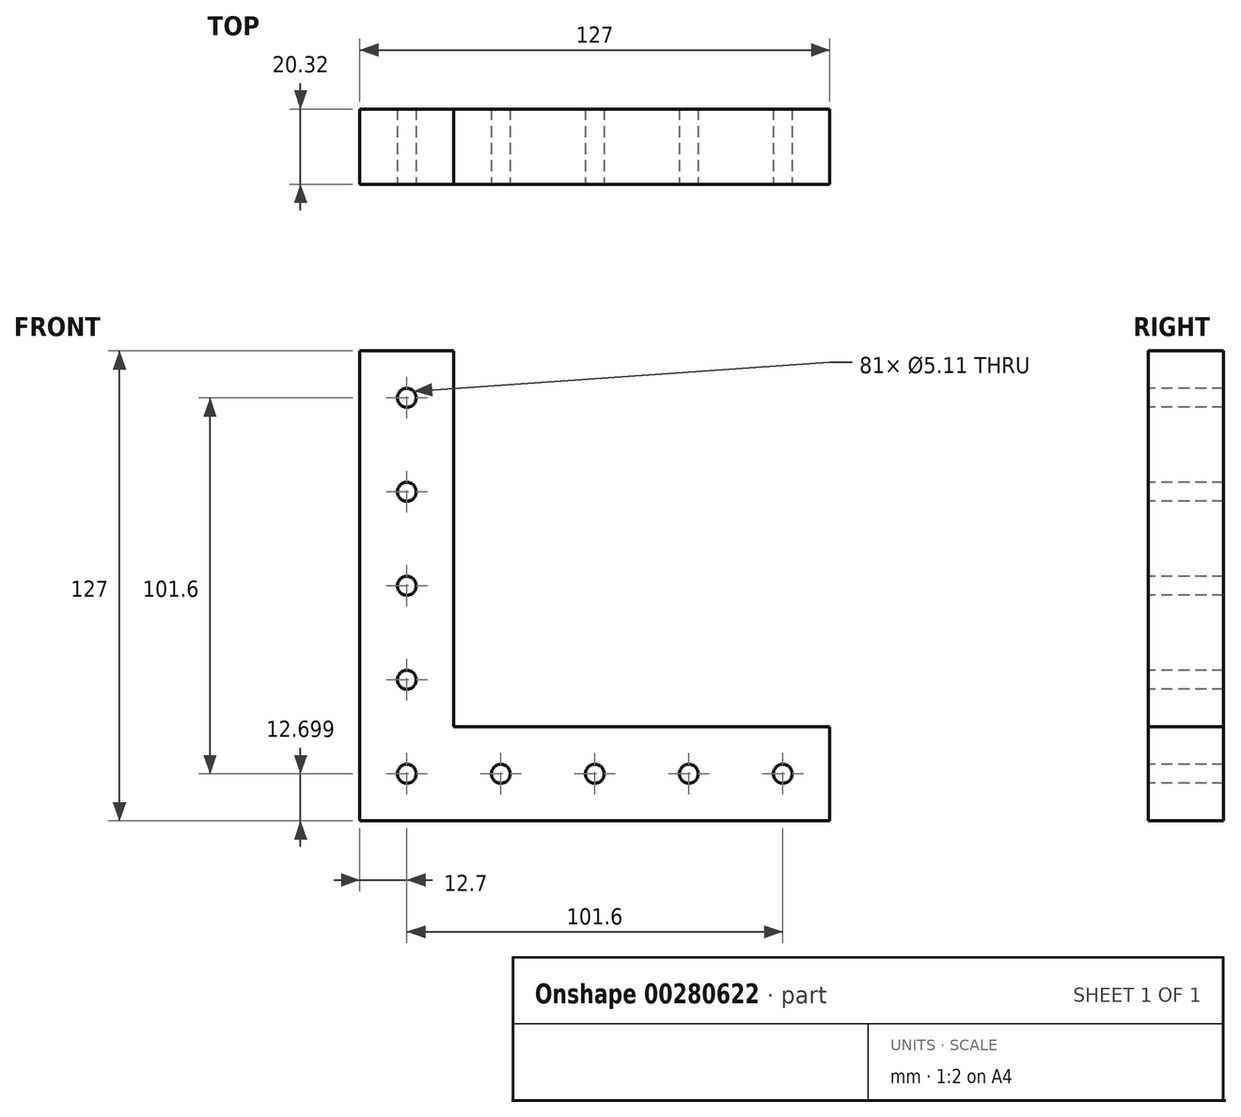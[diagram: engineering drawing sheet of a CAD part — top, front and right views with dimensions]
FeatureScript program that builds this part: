
annotation { "Feature Type Name" : "Feature", "Feature Type Description" : "" }
export const myFeature = defineFeature(function(context is Context, id is Id, definition is map)
    precondition{}
    {
        {
            var Q0;
            Q0=qCreatedBy(makeId("Front.planeOp"),FACE);
            var sketch = newSketch(context, id + "F0", { "sketchPlane" : qUnion([Q0])});
            skLineSegment(sketch, "E0", {"start": v(-127, 49.39) * mm, "end": v(-127, -77.61) * mm});
            skLineSegment(sketch, "E1", {"start": v(-127, -77.61) * mm, "end": v(0, -77.61) * mm});
            skLineSegment(sketch, "E2", {"start": v(0, -77.61) * mm, "end": v(0, -52.21) * mm});
            skLineSegment(sketch, "E3", {"start": v(0, -52.21) * mm, "end": v(-101.6, -52.21) * mm});
            skLineSegment(sketch, "E4", {"start": v(-101.6, -52.21) * mm, "end": v(-101.6, 49.39) * mm});
            skLineSegment(sketch, "E5", {"start": v(-101.6, 49.39) * mm, "end": v(-127, 49.39) * mm});
            skSolve(sketch);
        }
        {
            var Q0;
            Q0=makeQuery(id+"F0.imprint","IMPRINT",FACE,{"disambiguationData":[TD([[makeQuery(id+"F0.imprint","IMPRINT",EDGE,{"derivedFrom":sQuery(id+"F0.wireOp",EDGE,"E0")}),1.0]])]});
            extrude(context, id + "F1", {"entities" : qUnion([Q0]), "depth" : 20.32 * mm});
        }
        {
            var Q0;
            Q0=makeQuery(id+"F1.opExtrude","CAP_FACE",FACE,{"disambiguationData":[OSD([sQuery(id+"F0.wireOp",EDGE,"E0"),sQuery(id+"F0.wireOp",EDGE,"E1"),sQuery(id+"F0.wireOp",EDGE,"E2"),sQuery(id+"F0.wireOp",EDGE,"E3"),sQuery(id+"F0.wireOp",EDGE,"E4"),sQuery(id+"F0.wireOp",EDGE,"E5")])],"isStart":false});
            var sketch = newSketch(context, id + "F2", { "sketchPlane" : qUnion([Q0])});
            skCircle(sketch, "E6", {"center": v(-12.7, -64.91) * mm, "radius": 2.55 * mm});
            skCircle(sketch, "E7.1.0.0", {"center": v(-38.1, -64.91) * mm, "radius": 2.55 * mm});
            skCircle(sketch, "E7.2.0.0", {"center": v(-63.5, -64.91) * mm, "radius": 2.55 * mm});
            skCircle(sketch, "E7.3.0.0", {"center": v(-88.9, -64.91) * mm, "radius": 2.55 * mm});
            skCircle(sketch, "E7.4.0.0", {"center": v(-114.3, -64.91) * mm, "radius": 2.55 * mm});
            skLineSegment(sketch, "E7.direction1", {"start": v(-12.7, -64.91) * mm, "end": v(-38.1, -64.91) * mm, "construction": true});
            skLineSegment(sketch, "E7.direction2", {"start": v(-12.7, -64.91) * mm, "end": v(-12.7, -39.51) * mm, "construction": true});
            skCircle(sketch, "E8.0.1.0", {"center": v(-114.3, -39.51) * mm, "radius": 2.55 * mm});
            skCircle(sketch, "E8.0.2.0", {"center": v(-114.3, -14.11) * mm, "radius": 2.55 * mm});
            skCircle(sketch, "E8.0.3.0", {"center": v(-114.3, 11.29) * mm, "radius": 2.55 * mm});
            skCircle(sketch, "E8.0.4.0", {"center": v(-114.3, 36.69) * mm, "radius": 2.55 * mm});
            skLineSegment(sketch, "E8.direction1", {"start": v(-114.3, -64.91) * mm, "end": v(-88.9, -64.91) * mm, "construction": true});
            skLineSegment(sketch, "E8.direction2", {"start": v(-114.3, -64.91) * mm, "end": v(-114.3, -39.51) * mm, "construction": true});
            skSolve(sketch);
        }
        {
            var Q0;
            Q0=sQuery(id+"F2.wireOp",VERTEX,"E6.center");
            var Q1;
            Q1=sQuery(id+"F2.wireOp",VERTEX,"E7.4.0.0.center");
            var Q2;
            Q2=sQuery(id+"F2.wireOp",VERTEX,"E7.3.0.0.center");
            var Q3;
            Q3=sQuery(id+"F2.wireOp",VERTEX,"E7.2.0.0.center");
            var Q4;
            Q4=sQuery(id+"F2.wireOp",VERTEX,"E7.1.0.0.center");
            var Q5;
            Q5=sQuery(id+"F2.wireOp",VERTEX,"E8.0.3.0.center");
            var Q6;
            Q6=sQuery(id+"F2.wireOp",VERTEX,"E8.0.2.0.center");
            var Q7;
            Q7=sQuery(id+"F2.wireOp",VERTEX,"E8.0.1.0.center");
            var Q8;
            Q8=sQuery(id+"F2.wireOp",VERTEX,"E8.0.4.0.center");
            var Q9;
            Q9=makeQuery(id+"F1.opExtrude","SWEPT_BODY",BODY,{"disambiguationData":[OSD([sQuery(id+"F0.wireOp",EDGE,"E0"),sQuery(id+"F0.wireOp",EDGE,"E1"),sQuery(id+"F0.wireOp",EDGE,"E2"),sQuery(id+"F0.wireOp",EDGE,"E3"),sQuery(id+"F0.wireOp",EDGE,"E4"),sQuery(id+"F0.wireOp",EDGE,"E5")])]});
            hole(context, id + "F3", {"style" : HoleStyle.SIMPLE, "endStyle" : HoleEndStyle.THROUGH, "holeDiameter" : 5.1 * mm, "tappedDepth" : 12.7 * mm, "tapClearance" : 3, "locations" : qUnion([Q0, Q1, Q2, Q3, Q4, Q5, Q6, Q7, Q8]), "scope" : qUnion([Q9])});
        }
    });
